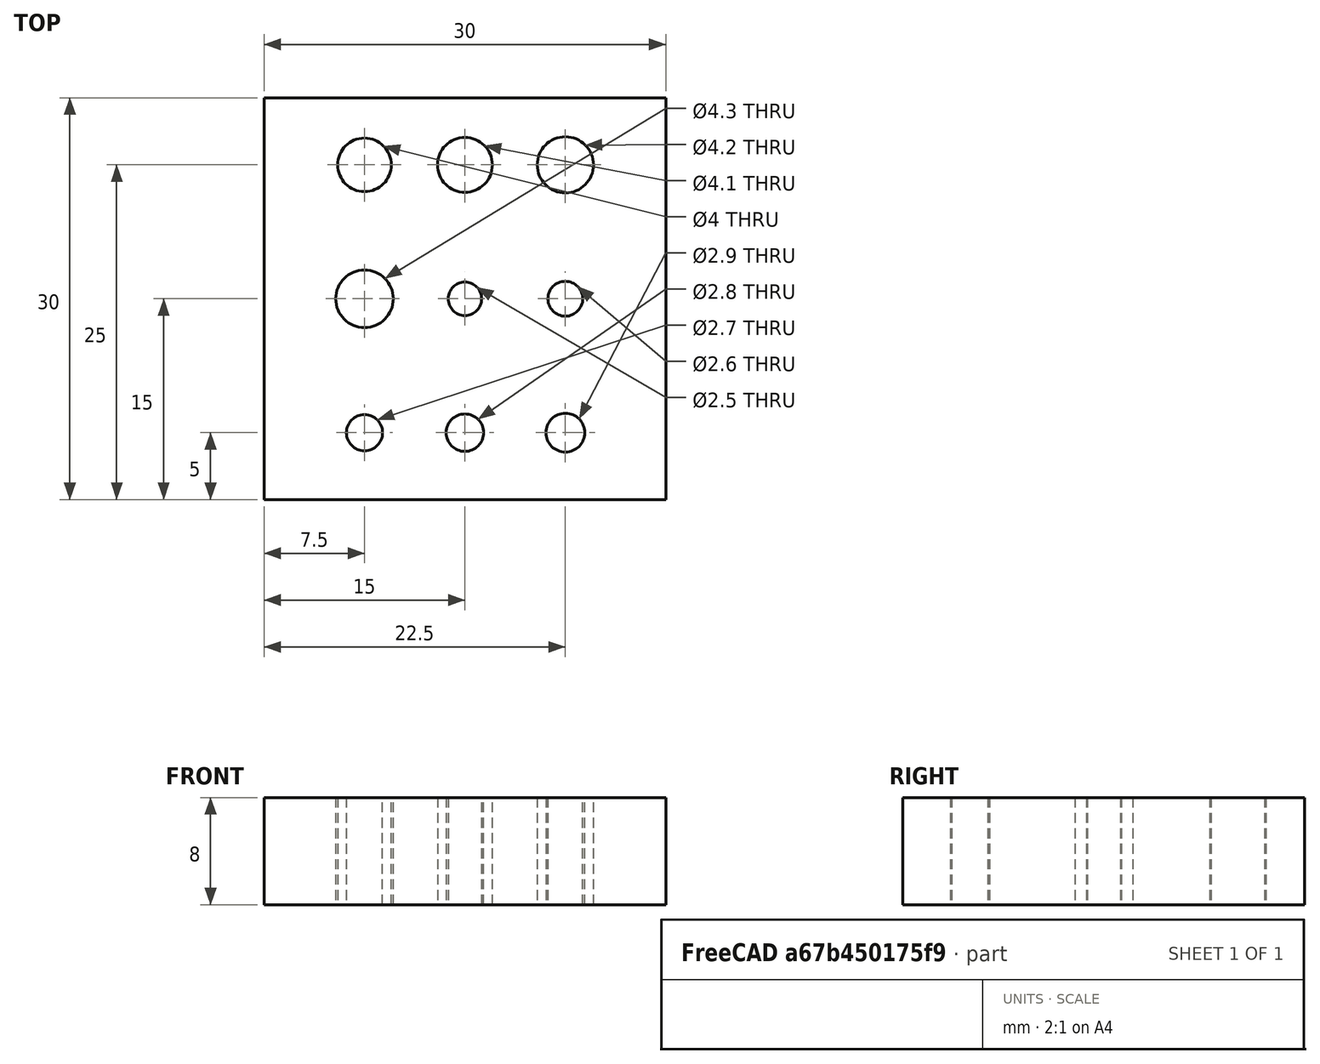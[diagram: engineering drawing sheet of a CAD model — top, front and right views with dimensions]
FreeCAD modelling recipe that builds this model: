
FCSTD DOCUMENT  (FreeCAD 1.0R39319 (Git))
Label: testinsert
License: All rights reserved
LicenseURL: https://en.wikipedia.org/wiki/All_rights_reserved
objects: Sketcher::SketchObject×1, PartDesign::Pad×1, PartDesign::Body×1
note: 6 computed .brp shape members not serialized (recipe doc carries the construction recipe); baked Part::Feature solids carry a one-line shape summary decoded from their .brp

FEATURE [Sketcher::SketchObject] Sketch
  ArcFitTolerance = 1e-06
  AttachmentSupport = -> [XY_Plane]
  FullyConstrained = true
  MakeInternals = false
  MapMode = 5
  sketch-geometry (18):
    g0: LineSegment StartX=15 StartY=-15 StartZ=0 EndX=15 EndY=15 EndZ=0
    g1: LineSegment StartX=15 StartY=15 StartZ=0 EndX=-15 EndY=15 EndZ=0
    g2: LineSegment StartX=-15 StartY=15 StartZ=0 EndX=-15 EndY=-15 EndZ=0
    g3: LineSegment StartX=-15 StartY=-15 StartZ=0 EndX=15 EndY=-15 EndZ=0
    g4: GeomPoint [constr] X=0 Y=0 Z=0
    g5: Circle CenterX=-7.5 CenterY=10 CenterZ=0 NormalX=0 NormalY=0 NormalZ=1 AngleXU=0 Radius=2
    g6: Circle CenterX=0 CenterY=10 CenterZ=0 NormalX=0 NormalY=0 NormalZ=1 AngleXU=0 Radius=2.05
    g7: Circle CenterX=7.5 CenterY=10 CenterZ=0 NormalX=0 NormalY=0 NormalZ=1 AngleXU=0 Radius=2.1
    g8: LineSegment [constr] StartX=-7.5 StartY=10 StartZ=0 EndX=7.5 EndY=10 EndZ=0
    g9: Circle CenterX=-7.5 CenterY=0 CenterZ=0 NormalX=0 NormalY=0 NormalZ=1 AngleXU=0 Radius=2.15
    g10: Circle CenterX=0 CenterY=0 CenterZ=0 NormalX=0 NormalY=0 NormalZ=1 AngleXU=0 Radius=1.25
    g11: Circle CenterX=7.5 CenterY=-10 CenterZ=0 NormalX=0 NormalY=0 NormalZ=1 AngleXU=0 Radius=1.45
    g12: Circle CenterX=0 CenterY=-10 CenterZ=0 NormalX=0 NormalY=0 NormalZ=1 AngleXU=0 Radius=1.4
    g13: Circle CenterX=-7.5 CenterY=-10 CenterZ=0 NormalX=0 NormalY=0 NormalZ=1 AngleXU=0 Radius=1.35
    g14: LineSegment [constr] StartX=-7.5 StartY=-10 StartZ=0 EndX=7.5 EndY=-10 EndZ=0
    g15: LineSegment [constr] StartX=-7.5 StartY=10 StartZ=0 EndX=-7.5 EndY=-10 EndZ=0
    g16: LineSegment [constr] StartX=7.5 StartY=10 StartZ=0 EndX=7.5 EndY=-10 EndZ=0
    g17: Circle CenterX=7.5 CenterY=0 CenterZ=0 NormalX=0 NormalY=0 NormalZ=1 AngleXU=0 Radius=1.3
  constraints (44):
    c: Coincident(g0,g1)
    c: Coincident(g1,g2)
    c: Coincident(g2,g3)
    c: Coincident(g3,g0)
    c: Vertical(g0)
    c: Vertical(g2)
    c: Horizontal(g1)
    c: Horizontal(g3)
    c: Symmetric(g2,g0,g4)
    c: Coincident(g4,g-1)
    c: DistanceY(g0,g0) = 30
    c: DistanceX(g1,g1) = 30
    c: PointOnObject(g6,g-2)
    c: Coincident(g8,g5)
    c: Coincident(g8,g7)
    c: PointOnObject(g6,g8)
    c: Symmetric(g7,g5,g-2)
    c: Diameter(g5) = 4
    c: Diameter(g6) = 4.1
    c: Diameter(g7) = 4.2
    c: DistanceX(g5,g7) = 15
    c: Distance(g7,g-1) = 10
    c: PointOnObject(g9,g-1)
    c: Coincident(g10,g4)
    c: PointOnObject(g12,g-2)
    c: Coincident(g14,g13)
    c: Coincident(g14,g11)
    c: PointOnObject(g12,g14)
    c: Horizontal(g14)
    c: Coincident(g15,g5)
    c: Coincident(g15,g13)
    c: Coincident(g16,g7)
    c: Coincident(g16,g11)
    c: Vertical(g16)
    c: Vertical(g15)
    c: PointOnObject(g9,g15)
    c: Symmetric(g16,g16,g17)
    c: Diameter(g9) = 4.3
    c: Diameter(g10) = 2.5
    c: Diameter(g17) = 2.6
    c: Diameter(g13) = 2.7
    c: Diameter(g12) = 2.8
    c: Diameter(g11) = 2.9
    c: PointOnObject(g17,g-1)
FEATURE [PartDesign::Pad] Pad
  Direction = (0,0,1)
  Length = 8
  Length2 = 10
  Profile = -> Sketch
  ReferenceAxis = -> Sketch [N_Axis]
  Refine = true
  Suppressed = false
  Type = 0
FEATURE [PartDesign::Body] Body  label="Corps"
  AllowCompound = false
  Group = -> [Sketch,Pad]
  Origin = -> Origin
  Tip = -> Pad
